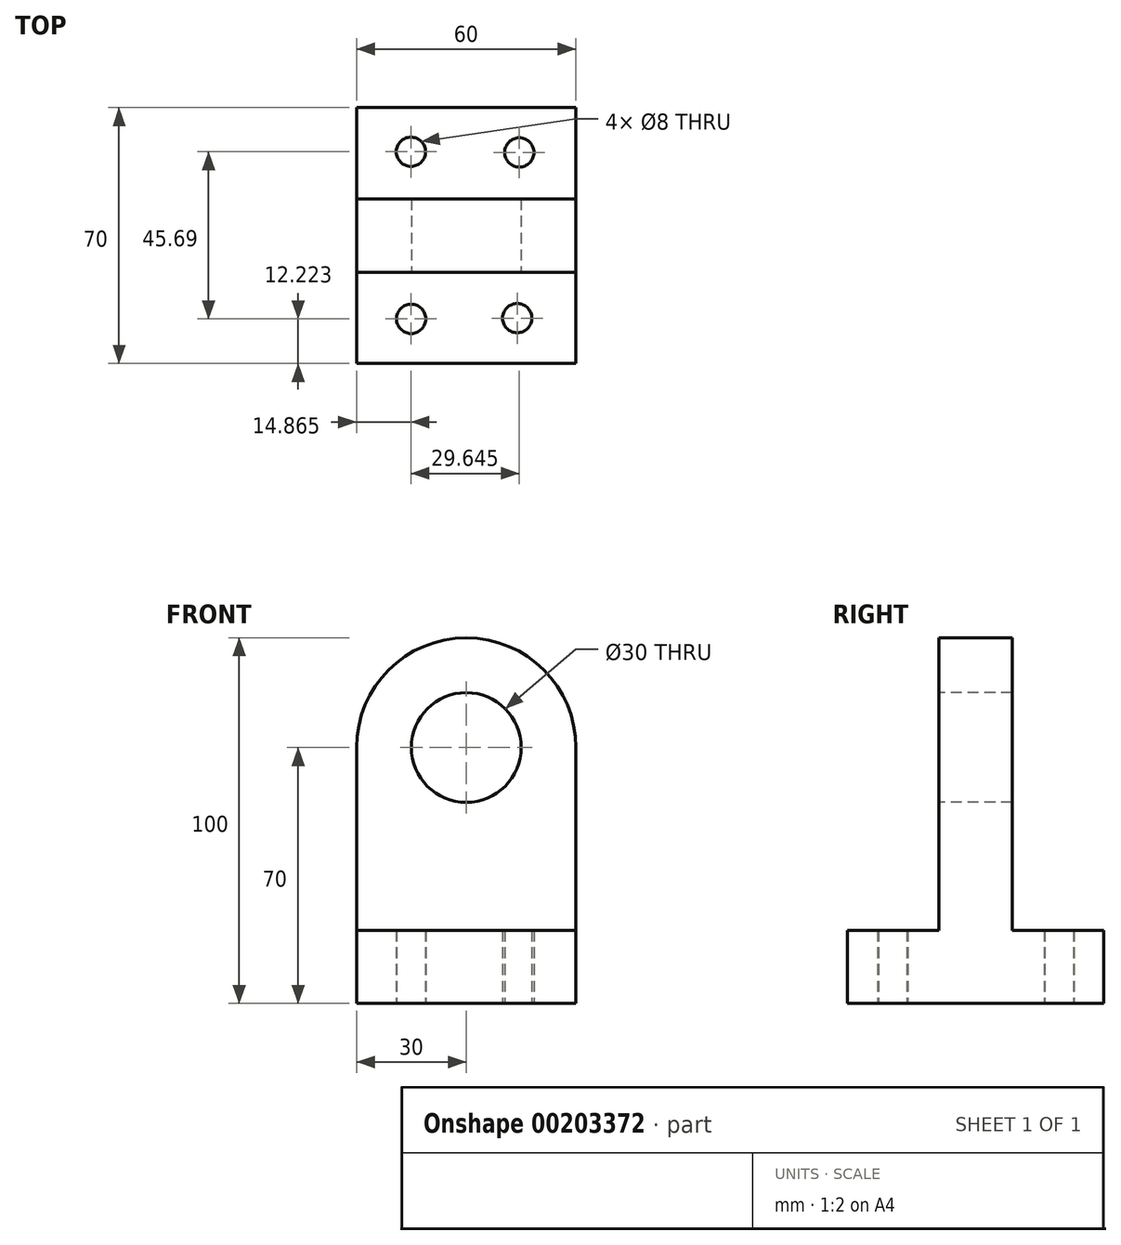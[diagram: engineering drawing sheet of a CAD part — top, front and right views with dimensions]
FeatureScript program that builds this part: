
annotation { "Feature Type Name" : "Feature", "Feature Type Description" : "" }
export const myFeature = defineFeature(function(context is Context, id is Id, definition is map)
    precondition{}
    {
        {
            var Q0;
            Q0=qCreatedBy(makeId("Top.planeOp"),FACE);
            var sketch = newSketch(context, id + "F0", { "sketchPlane" : qUnion([Q0])});
            skLineSegment(sketch, "E0.bottom", {"start": v(-30, 35) * mm, "end": v(30, 35) * mm});
            skLineSegment(sketch, "E0.top", {"start": v(-30, -35) * mm, "end": v(30, -35) * mm});
            skLineSegment(sketch, "E0.left", {"start": v(-30, 35) * mm, "end": v(-30, -35) * mm});
            skLineSegment(sketch, "E0.right", {"start": v(30, 35) * mm, "end": v(30, -35) * mm});
            skSolve(sketch);
        }
        {
            var Q0;
            Q0=makeQuery(id+"F0.imprint","IMPRINT",FACE,{"disambiguationData":[TD([[makeQuery(id+"F0.imprint","IMPRINT",EDGE,{"derivedFrom":sQuery(id+"F0.wireOp",EDGE,"E0.bottom")}),-1.0]])]});
            extrude(context, id + "F1", {"entities" : qUnion([Q0]), "depth" : 20 * mm});
        }
        {
            var Q0;
            Q0=qCreatedBy(makeId("Front.planeOp"),FACE);
            var sketch = newSketch(context, id + "F2", { "sketchPlane" : qUnion([Q0])});
            skLineSegment(sketch, "E1.bottom", {"start": v(-30, 20) * mm, "end": v(30, 20) * mm});
            skLineSegment(sketch, "E1.left", {"start": v(-30, 20) * mm, "end": v(-30, 70) * mm});
            skLineSegment(sketch, "E1.right", {"start": v(30, 20) * mm, "end": v(30, 70) * mm});
            skPoint(sketch, "E2.center.orphan", {"position": v(0, 70) * mm});
            skArc(sketch, "E3", {"start": v(30, 70) * mm, "mid": v(0, 100) * mm, "end": v(-30, 70) * mm});
            skSolve(sketch);
        }
        {
            var Q0;
            Q0 = qSketchRegion(id + "F2", true);
            extrude(context, id + "F3", {"entities" : qUnion([Q0]), "operationType" : NewBodyOperationType.ADD, "depth" : 10 * mm, "hasSecondDirection" : true, "secondDirectionOppositeDirection" : true, "secondDirectionDepth" : 10 * mm});
        }
        {
            var Q0;
            Q0=sQuery(id+"F2.wireOp",VERTEX,"E2.center.orphan");
            var Q1;
            Q1=makeQuery(id+"F1.opExtrude","SWEPT_BODY",BODY,{"disambiguationData":[OSD([sQuery(id+"F0.wireOp",EDGE,"E0.bottom"),sQuery(id+"F0.wireOp",EDGE,"E0.top"),sQuery(id+"F0.wireOp",EDGE,"E0.left"),sQuery(id+"F0.wireOp",EDGE,"E0.right")])]});
            hole(context, id + "F4", {"style" : HoleStyle.SIMPLE, "endStyle" : HoleEndStyle.THROUGH, "holeDiameter" : 30 * mm, "locations" : qUnion([Q0]), "scope" : qUnion([Q1]), "isTappedThrough" : true});
        }
        {
            var Q0;
            Q0=sQuery(id+"F2.wireOp",VERTEX,"E2.center.orphan");
            var Q1;
            Q1=makeQuery(id+"F1.opExtrude","SWEPT_BODY",BODY,{"disambiguationData":[OSD([sQuery(id+"F0.wireOp",EDGE,"E0.bottom"),sQuery(id+"F0.wireOp",EDGE,"E0.top"),sQuery(id+"F0.wireOp",EDGE,"E0.left"),sQuery(id+"F0.wireOp",EDGE,"E0.right")])]});
            hole(context, id + "F5", {"style" : HoleStyle.SIMPLE, "endStyle" : HoleEndStyle.THROUGH, "oppositeDirection" : true, "holeDiameter" : 30 * mm, "locations" : qUnion([Q0]), "scope" : qUnion([Q1]), "isTappedThrough" : true});
        }
        {
            var Q0;
            Q0=qCreatedBy(makeId("Top.planeOp"),FACE);
            var sketch = newSketch(context, id + "F6", { "sketchPlane" : qUnion([Q0])});
            skCircle(sketch, "E4", {"center": v(-15.08, -22.78) * mm, "radius": 4 * mm});
            skSolve(sketch);
        }
        {
            var Q0;
            Q0=sQuery(id+"F6.wireOp",VERTEX,"E4.center");
            var Q1;
            Q1=makeQuery(id+"F1.opExtrude","SWEPT_BODY",BODY,{"disambiguationData":[OSD([sQuery(id+"F0.wireOp",EDGE,"E0.bottom"),sQuery(id+"F0.wireOp",EDGE,"E0.top"),sQuery(id+"F0.wireOp",EDGE,"E0.left"),sQuery(id+"F0.wireOp",EDGE,"E0.right")])]});
            hole(context, id + "F7", {"style" : HoleStyle.SIMPLE, "endStyle" : HoleEndStyle.THROUGH, "oppositeDirection" : true, "holeDiameter" : 8 * mm, "locations" : qUnion([Q0]), "scope" : qUnion([Q1]), "isTappedThrough" : true});
        }
        {
            var Q0;
            Q0=qCreatedBy(makeId("Top.planeOp"),FACE);
            var sketch = newSketch(context, id + "F8", { "sketchPlane" : qUnion([Q0])});
            skCircle(sketch, "E5", {"center": v(13.94, -22.58) * mm, "radius": 4 * mm});
            skSolve(sketch);
        }
        {
            var Q0;
            Q0=sQuery(id+"F8.wireOp",VERTEX,"E5.center");
            var Q1;
            Q1=makeQuery(id+"F1.opExtrude","SWEPT_BODY",BODY,{"disambiguationData":[OSD([sQuery(id+"F0.wireOp",EDGE,"E0.bottom"),sQuery(id+"F0.wireOp",EDGE,"E0.top"),sQuery(id+"F0.wireOp",EDGE,"E0.left"),sQuery(id+"F0.wireOp",EDGE,"E0.right")])]});
            hole(context, id + "F9", {"style" : HoleStyle.SIMPLE, "endStyle" : HoleEndStyle.THROUGH, "oppositeDirection" : true, "holeDiameter" : 8 * mm, "locations" : qUnion([Q0]), "scope" : qUnion([Q1]), "isTappedThrough" : true});
        }
        {
            var Q0;
            Q0=qCreatedBy(makeId("Top.planeOp"),FACE);
            var sketch = newSketch(context, id + "F10", { "sketchPlane" : qUnion([Q0])});
            skCircle(sketch, "E6", {"center": v(14.51, 22.74) * mm, "radius": 4 * mm});
            skSolve(sketch);
        }
        {
            var Q0;
            Q0=sQuery(id+"F10.wireOp",VERTEX,"E6.center");
            var Q1;
            Q1=makeQuery(id+"F1.opExtrude","SWEPT_BODY",BODY,{"disambiguationData":[OSD([sQuery(id+"F0.wireOp",EDGE,"E0.bottom"),sQuery(id+"F0.wireOp",EDGE,"E0.top"),sQuery(id+"F0.wireOp",EDGE,"E0.left"),sQuery(id+"F0.wireOp",EDGE,"E0.right")])]});
            hole(context, id + "F11", {"style" : HoleStyle.SIMPLE, "endStyle" : HoleEndStyle.THROUGH, "oppositeDirection" : true, "holeDiameter" : 8 * mm, "locations" : qUnion([Q0]), "scope" : qUnion([Q1]), "isTappedThrough" : true});
        }
        {
            var Q0;
            Q0=qCreatedBy(makeId("Top.planeOp"),FACE);
            var sketch = newSketch(context, id + "F12", { "sketchPlane" : qUnion([Q0])});
            skCircle(sketch, "E7", {"center": v(-15.13, 22.91) * mm, "radius": 4 * mm});
            skSolve(sketch);
        }
        {
            var Q0;
            Q0=sQuery(id+"F12.wireOp",VERTEX,"E7.center");
            var Q1;
            Q1=makeQuery(id+"F1.opExtrude","SWEPT_BODY",BODY,{"disambiguationData":[OSD([sQuery(id+"F0.wireOp",EDGE,"E0.bottom"),sQuery(id+"F0.wireOp",EDGE,"E0.top"),sQuery(id+"F0.wireOp",EDGE,"E0.left"),sQuery(id+"F0.wireOp",EDGE,"E0.right")])]});
            hole(context, id + "F13", {"style" : HoleStyle.SIMPLE, "endStyle" : HoleEndStyle.THROUGH, "oppositeDirection" : true, "holeDiameter" : 8 * mm, "locations" : qUnion([Q0]), "scope" : qUnion([Q1]), "isTappedThrough" : true});
        }
    });
